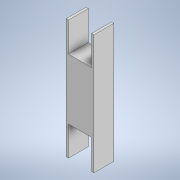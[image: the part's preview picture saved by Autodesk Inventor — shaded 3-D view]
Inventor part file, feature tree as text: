
AUTODESK INVENTOR PART (.ipt)
format: ipt  version: 2020 (Build 240168000, 168)  size: 127,488 bytes
history: native  units: mm
features: extrude x2, sketch x1
ambient origin geometry x8: Origin, YZ Plane, XZ Plane, XY Plane, X Axis, Y Axis, Z Axis, Center Point
bodies: Solid1 (feature_tree)
feature tree (3):
  extrude  "Extrusion1"  Depth=80.0mm
  extrude  "Extrusion2"  Depth=80.0mm
  sketch  "Sketch2"  dims[d0=70.0mm d1=80.0mm d2=80.0mm d3=6.0mm d4=50.0mm d5=0.0mm d7=6.0mm d8=140.0mm d9=0.0mm d10=70.0mm d6=0.5mm]
